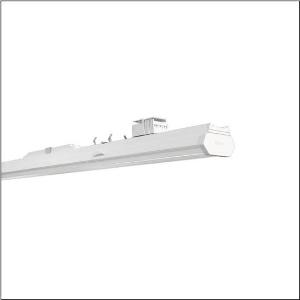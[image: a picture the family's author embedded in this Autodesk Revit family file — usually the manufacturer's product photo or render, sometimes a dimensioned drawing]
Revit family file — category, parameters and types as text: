
# Revit family: licross_r__11_protected_mo_51tp11cn58xf_4d9e
name_source: partatom
category: Lighting Fixtures
units: mm (PartAtom-declared; Revit-internal decimal feet)

## family parameters
Cut with Voids When Loaded = No
Host = Face
Light Source = No
Part Type = Normal
Room Calculation Point = No
Round Connector Dimension = Use Diameter
Shared = No

## types (1)
- --- (1 x LED, 8150 lm, 49 W, 5000K)
    Apparent Load = 49 VA
    CIE Flux Codes = 83 94 98 100 100
    Color Rendering = 80
    Color Temperature = 5000K
    Default Elevation = 1800 mm
    Description = Licross® 11 Protected MO, luminaire insert, of sheet steel, galvanised, coil coated, white, length: 1.500mm, width: 90mm, height: 101mm, LED rated luminous flux: 8.150lm, light colour: 850, control gear: ON/OFF Multilumen, CLOi, control gear: ECG Multilumen, with plug, 3-pole, with phase selection, mains connection: 220..240V, AC, 50/60Hz, start of lifetime: 49W, end of service life: 54W, halogen-free wiring, primary optical cover: cover, of PMMA, light emission: direct distribution, primary light characteristic: symmetric, protection rating (complete): IP64, insulation class (complete): insulation class I (protective earthing), certification: CE, ENEC, VDE, UKCA, protection symbol: D if used in an environment with conductive dust loads with corresponding accessories, impact resistance: IK06, permissible ambient temperature for indoor applications: -35..+40°C, corresponds to IFS (International Featured Standards) requirements for safety and quality in the food industry, reducing of maximum allowable ambient temperature of 5°C with ceiling mounting, LABS conformity tested according to VDMA 24364:2018-05, packaging unit: 1 piece
    Height = 92 mm
    Lamp = 1 x LED
    Lamp Light Flux = 8150 lm
    Lamp Power = 49 W
    Lamp count = 1
    Length = 1500 mm
    Luminous efficacy = 166 lm/W
    Manufacturer = Siteco
    ModVariant = No
    Model = 51TP11CN58XF
    Mounting Place = Ceiling
    Mounting Type = Pendant
    Number of Poles = 1
    OnlyDefault = Yes
    Power Factor = 1
    Product Name = Licross® 11 Protected MO
    Product group = luminaire insert
    ProductGroupID = 901
    Protection Class = Protection class I
    Protection Degree = IP 64
    RLX_Detail_Level = 1
    RLX_Emergency_Light_Flux = 0 lm
    RLX_Emergency_Type = 0
    RLX_Emergency_Type_DB = No
    RlxData = <blob elided: 21729 chars, md5=7b942ffb>
    Socket = socket
    Standby Power = 0 W
    System Light Flux = 8150 lm
    System Power = 49 W
    Type Comments = factory setting: luminous flux: 100 % | (A | C | E) | 111 mA
    Type Image = l_1256148.jpg
    URL = http://relux.com
    VarID = @adj_143469
    Voltage = 0 V
    Weight = 0.00 kg
    Width = 88 mm

## geometry (parser evidence)
native form markers: Blend x4, Sweep x10
no freeform markers — native parametric forms only
